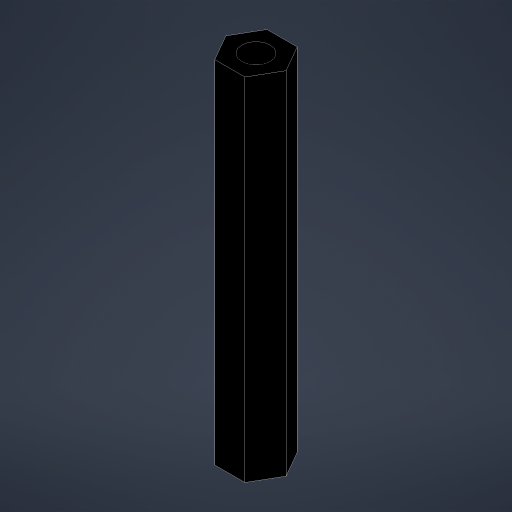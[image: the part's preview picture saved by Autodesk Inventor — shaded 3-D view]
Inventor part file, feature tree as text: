
AUTODESK INVENTOR PART (.ipt)
format: ipt  version: 2024.1 (Build 281209000, 209)  size: 171,520 bytes
history: native  units: mm
features: extrude x1, sketch x1
ambient origin geometry x8: Origin, YZ Plane, XZ Plane, XY Plane, X Axis, Y Axis, Z Axis, Center Point
bodies: Solid1 (feature_tree)
feature tree (2):
  extrude  "Extrusion1"  Depth=37.0mm
  sketch  "Sketch1"  dims[d0=5.5mm d1=3.0mm d2=37.0mm d3=0.0mm d4=0.5mm d5=0.872665mm]
